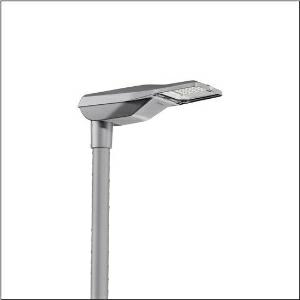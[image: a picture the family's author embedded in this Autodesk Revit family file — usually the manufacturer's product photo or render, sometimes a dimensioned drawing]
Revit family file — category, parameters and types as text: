
# Revit family: streetlight_sl_21_iq_micro___st0_8a_5xe1c31d08db_b6ee
name_source: partatom
category: Lighting Fixtures
units: mm (PartAtom-declared; Revit-internal decimal feet)

## family parameters
Cut with Voids When Loaded = No
Host = Face
Light Source = No
Part Type = Normal
Room Calculation Point = No
Round Connector Dimension = Use Diameter
Shared = No

## types (1)
- --- (1 x LED, 4810 lm, 36.4 W, 3000K)
    Apparent Load = 36 VA
    CIE Flux Codes = 38 75 97 100 100
    Color Rendering = 70
    Color Temperature = 3000K
    Default Elevation = 1800 mm
    Description = Streetlight SL 21 iQ micro, mast luminaire, primary light control with lens, of PMMA, primary optical cover: cover, of toughened safety glass, transparent, light distribution: ST0.8a, light emission: direct distribution, primary light characteristic: asymmetric, installation type: post-top, side-entry, LED, High Power LED, rated luminous flux: 4.810lm, luminous efficacy: 132lm/W, light colour: 730, colour temperature: 3000K, control gear: iQ-Comfort, control: Auto-Match, Temp-Guard, Lumen-Switch, Night-Set, Smart-Wire, Light-Fading, Desk-Remote (wireless, voltage-free reading and setting of iQ features in the workshop via application-optimized NFC function/RFID function), optimised constant luminous flux control (CLO 2.0), pre-setting: linear dimming characteristic, mains connection: 220..240V, AC, 50/60Hz, start of lifetime: 36W, end of service life: 38W, reduction: 16W, luminaire housing, of diecast aluminium, powder-coated, SITECO metallic grey (DB 702S), corrosivity category C5 high according to DIN EN ISO 12944, please order mast flange separately, inclination adjustable: 0°, 5°, 10°, 15°, sealing non-destructively replaceable, multi-level sealing system, length: 528mm, width: 235mm, height: 110mm, mast flange for spigot size: 42mm (side-entry): 5XC10008XM4, 60/48mm (side-entry/post-top): 5XC10108XM2, 76/60mm (side-entry/post-top): 5XC10108XM1, protection rating (complete): IP66, insulation class (complete): insulation class II (safety insulation), certification: CE, ENEC, ENEC+, VDE, impact resistance: IK10, permissible operating ambient temperature for outdoor applications: -40..+50°C, standard-compliant lighting for roads and squares, packaging unit: 1 piece

Light Distribution: ST0.8a
    Height = 110 mm
    Lamp = 1 x LED
    Lamp Light Flux = 4810 lm
    Lamp Power = 36.4 W
    Lamp count = 1
    Length = 528 mm
    Luminous efficacy = 132 lm/W
    Manufacturer = Siteco
    ModVariant = No
    Model = 5XE1C31D08DB
    Number of Poles = 1
    OnlyDefault = Yes
    Power Factor = 1
    Product Name = Streetlight SL 21 iQ micro | ST0.8a
    Product group = mast luminaire | pylon top
    ProductGroupID = 6100
    Protection Class = Protection class II
    Protection Degree = IP 66
    RLX_Detail_Level = 1
    RLX_Emergency_Light_Flux = 0 lm
    RLX_Emergency_Type = 0
    RLX_Emergency_Type_DB = No
    RlxData = <blob elided: 99357 chars, md5=aa4d4802>
    Socket = socket
    Standby Power = 0 W
    System Light Flux = 4810 lm
    System Power = 36 W
    Type Comments = factory setting: luminous flux: 100 % | dim-lin: 254 | 715 mA
    Type Image = l_1006881.jpg
    URL = http://relux.com
    VarID = @adj_154071
    Voltage = 0 V
    Weight = 0.00 kg
    Width = 235 mm

## geometry (parser evidence)
native form markers: Blend x4, Sweep x10
no freeform markers — native parametric forms only
